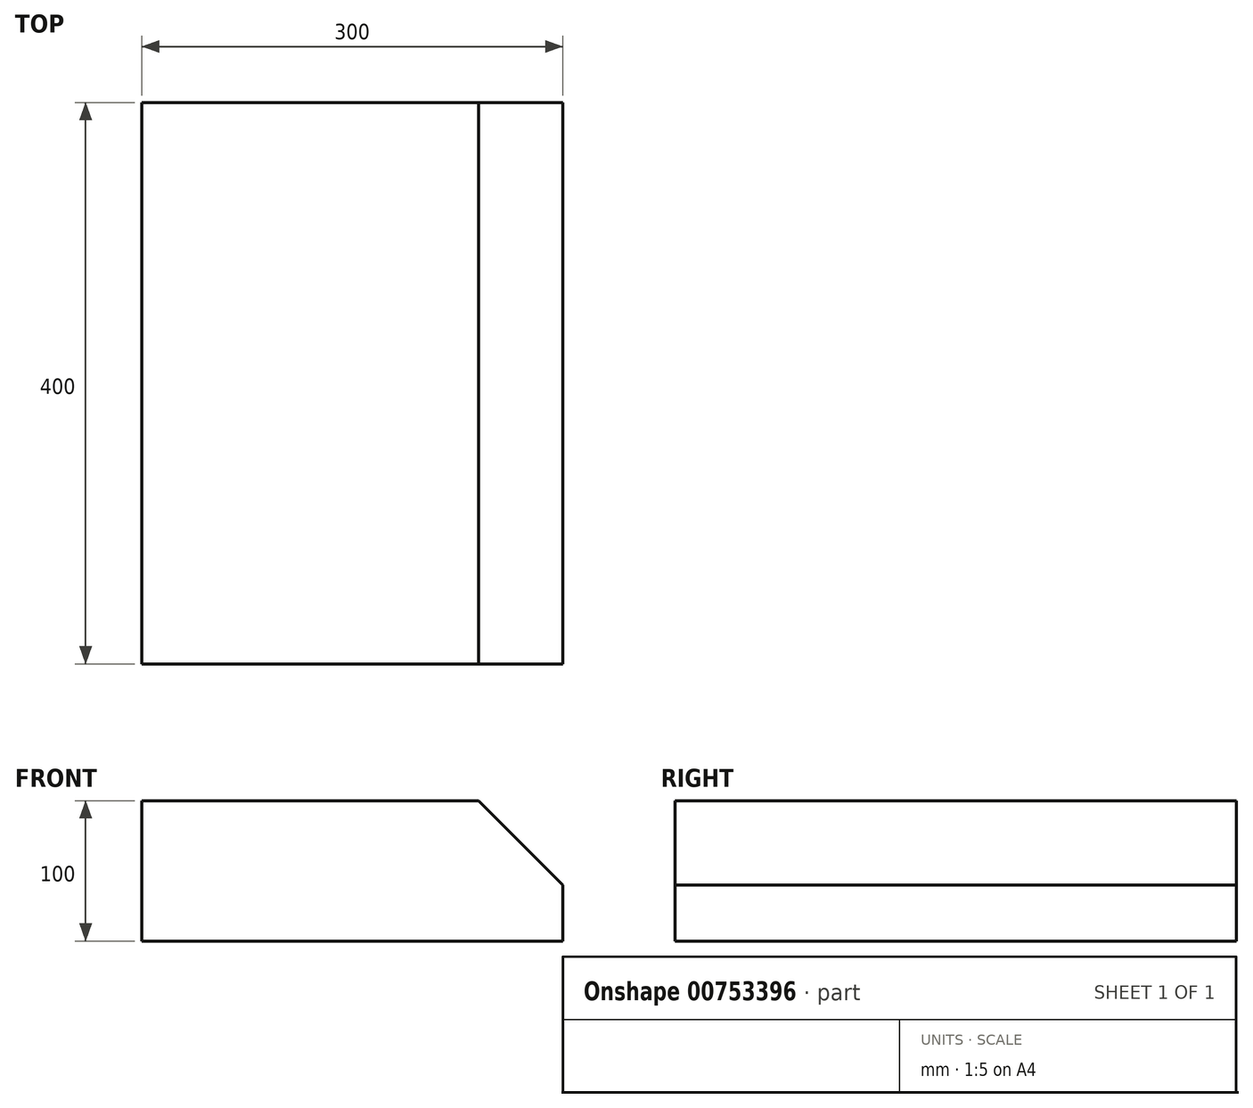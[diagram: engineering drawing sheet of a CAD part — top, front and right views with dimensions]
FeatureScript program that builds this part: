
annotation { "Feature Type Name" : "Feature", "Feature Type Description" : "" }
export const myFeature = defineFeature(function(context is Context, id is Id, definition is map)
    precondition{}
    {
        {
            var Q0;
            Q0=qCreatedBy(makeId("Front.planeOp"),FACE);
            var sketch = newSketch(context, id + "F0", { "sketchPlane" : qUnion([Q0])});
            skLineSegment(sketch, "E0", {"start": v(0, 0) * mm, "end": v(300, 0) * mm});
            skLineSegment(sketch, "E1", {"start": v(300, 0) * mm, "end": v(300, 40) * mm});
            skLineSegment(sketch, "E2", {"start": v(300, 40) * mm, "end": v(240, 100) * mm});
            skLineSegment(sketch, "E3", {"start": v(240, 100) * mm, "end": v(0, 100) * mm});
            skLineSegment(sketch, "E4", {"start": v(0, 100) * mm, "end": v(0, 0) * mm});
            skSolve(sketch);
        }
        {
            var Q0;
            Q0 = qSketchRegion(id + "F0", true);
            extrude(context, id + "F1", {"entities" : qUnion([Q0]), "endBound" : BoundingType.SYMMETRIC, "depth" : 400 * mm, "offsetDistance" : 25 * mm});
        }
    });
